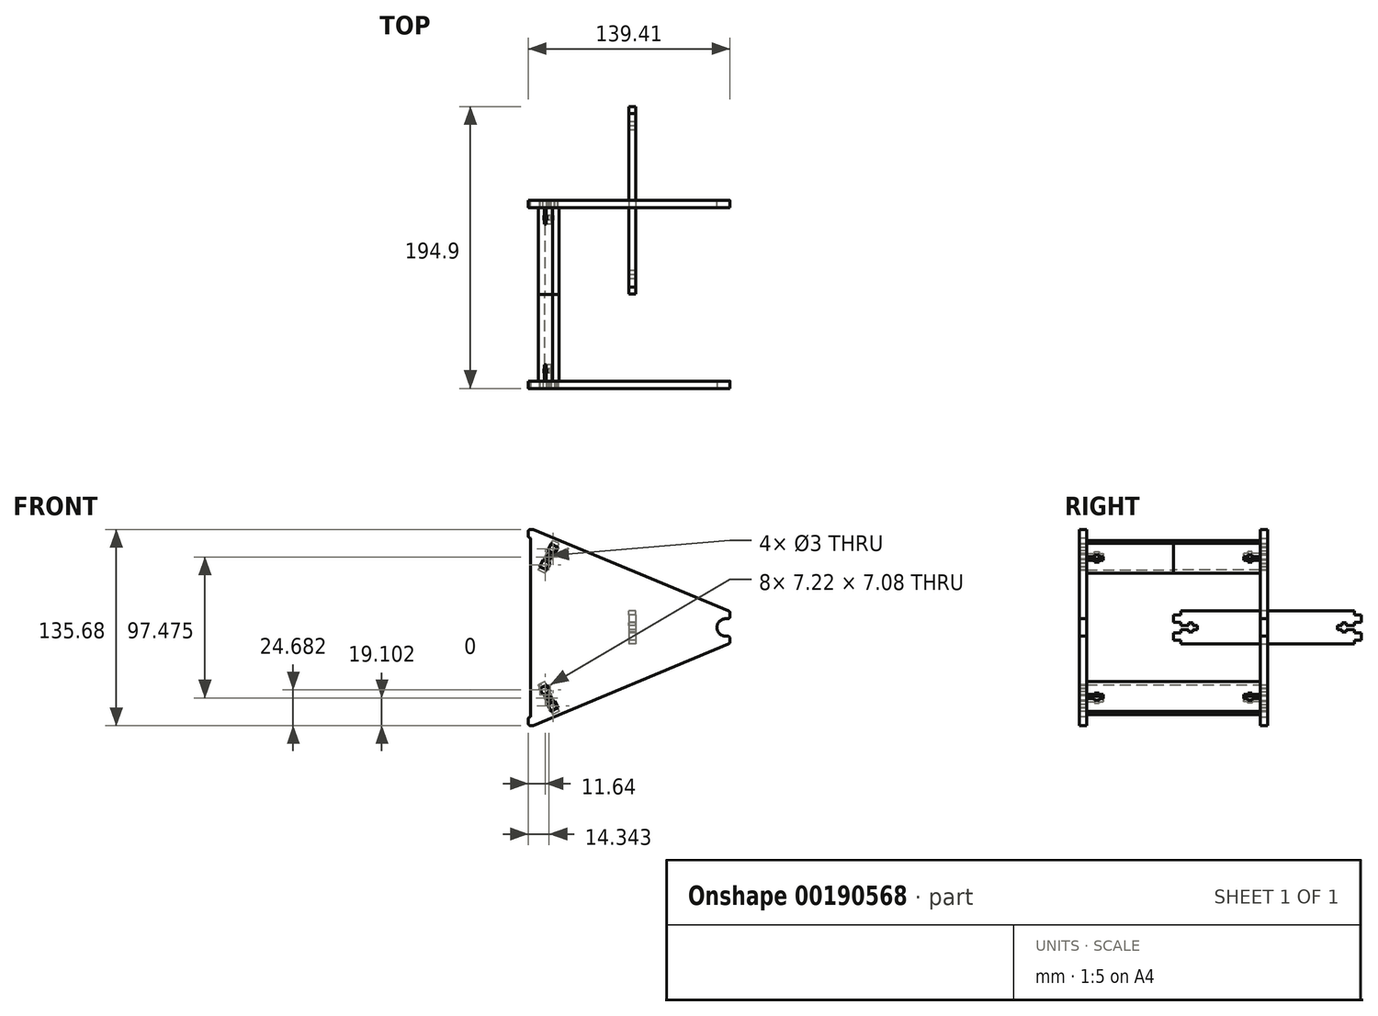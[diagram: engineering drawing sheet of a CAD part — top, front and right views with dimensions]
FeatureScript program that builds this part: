
annotation { "Feature Type Name" : "Feature", "Feature Type Description" : "" }
export const myFeature = defineFeature(function(context is Context, id is Id, definition is map)
    precondition{}
    {
        {
            var Q0;
            Q0=qCreatedBy(makeId("Front.planeOp"),FACE);
            var sketch = newSketch(context, id + "F0", { "sketchPlane" : qUnion([Q0])});
            skLineSegment(sketch, "E0.bottom", {"start": v(70, 69) * mm, "end": v(-70, 69) * mm, "construction": true});
            skLineSegment(sketch, "E0.top", {"start": v(70, -69) * mm, "end": v(-70, -69) * mm, "construction": true});
            skLineSegment(sketch, "E0.left", {"start": v(70, 69) * mm, "end": v(70, -69) * mm, "construction": true});
            skLineSegment(sketch, "E0.right", {"start": v(-70, 69) * mm, "end": v(-70, -69) * mm, "construction": true});
            skPoint(sketch, "E0.middle", {"position": v(0, 0) * mm});
            skLineSegment(sketch, "E1", {"start": v(-67.9, 67.84) * mm, "end": v(-66.66, 67.84) * mm});
            skLineSegment(sketch, "E2", {"start": v(-66.08, 67.72) * mm, "end": v(69.08, 11.47) * mm});
            skArc(sketch, "E3", {"start": v(67, 6) * mm, "mid": v(62.76, 4.24) * mm, "end": v(61, 0) * mm});
            skLineSegment(sketch, "E4", {"start": v(67, 6) * mm, "end": v(68.5, 6) * mm});
            skLineSegment(sketch, "E5", {"start": v(70, 7.5) * mm, "end": v(70, 10.09) * mm});
            skLineSegment(sketch, "E6", {"start": v(73.6, 0) * mm, "end": v(46.28, 0) * mm, "construction": true});
            skPoint(sketch, "E6.startSnap0", {"position": v(70, 0) * mm});
            skCircle(sketch, "E7", {"center": v(67, 0) * mm, "radius": 6 * mm, "construction": true});
            skCircle(sketch, "E8", {"center": v(45.57, 0) * mm, "radius": 27.5 * mm, "construction": true});
            skCircle(sketch, "E9", {"center": v(45.57, 0) * mm, "radius": 100 * mm, "construction": true});
            skLineSegment(sketch, "E10", {"start": v(-69.4, 66.34) * mm, "end": v(-69.4, 63.34) * mm});
            skLineSegment(sketch, "E11", {"start": v(-67.9, 61.84) * mm, "end": v(-67.9, 61.84) * mm});
            skLineSegment(sketch, "E12", {"start": v(-67.9, 61.84) * mm, "end": v(-67.9, 0) * mm});
            skPoint(sketch, "E13.visualSharp", {"position": v(70, 11.09) * mm});
            skArc(sketch, "E13.filletArc", {"start": v(70, 10.09) * mm, "mid": v(69.75, 10.92) * mm, "end": v(69.08, 11.47) * mm});
            skPoint(sketch, "E14.visualSharp", {"position": v(70, 6) * mm});
            skArc(sketch, "E14.filletArc", {"start": v(68.5, 6) * mm, "mid": v(69.56, 6.44) * mm, "end": v(70, 7.5) * mm});
            skPoint(sketch, "E15.visualSharp", {"position": v(-69.4, 67.84) * mm});
            skArc(sketch, "E15.filletArc", {"start": v(-67.9, 67.84) * mm, "mid": v(-68.97, 67.4) * mm, "end": v(-69.4, 66.34) * mm});
            skPoint(sketch, "E16.visualSharp", {"position": v(-69.4, 61.84) * mm});
            skArc(sketch, "E16.filletArc", {"start": v(-69.4, 63.34) * mm, "mid": v(-68.97, 62.27) * mm, "end": v(-67.9, 61.84) * mm});
            skPoint(sketch, "E17.visualSharp", {"position": v(-66.36, 67.84) * mm});
            skArc(sketch, "E17.filletArc", {"start": v(-66.08, 67.72) * mm, "mid": v(-66.37, 67.8) * mm, "end": v(-66.66, 67.84) * mm});
            skLineSegment(sketch, "E18", {"start": v(-48.76, 55.46) * mm, "end": v(-51.02, 50.78) * mm});
            skLineSegment(sketch, "E19", {"start": v(-37.94, 57) * mm, "end": v(-56.8, 18.07) * mm, "construction": true});
            skLineSegment(sketch, "E20", {"start": v(-48.76, 55.46) * mm, "end": v(-53.7, 57.86) * mm});
            skLineSegment(sketch, "E21", {"start": v(-56.43, 39.62) * mm, "end": v(-61.38, 42.02) * mm});
            skLineSegment(sketch, "E22", {"start": v(-53.7, 57.86) * mm, "end": v(-55.97, 53.18) * mm});
            skLineSegment(sketch, "E23", {"start": v(-57.54, 49.94) * mm, "end": v(-52.6, 47.54) * mm, "construction": true});
            skCircle(sketch, "E24", {"center": v(-55.07, 48.74) * mm, "radius": 1.5 * mm});
            skLineSegment(sketch, "E25", {"start": v(-55.97, 53.18) * mm, "end": v(-51.02, 50.78) * mm});
            skLineSegment(sketch, "E26.MirrorCS", {"start": v(-59.11, 46.7) * mm, "end": v(-54.16, 44.3) * mm});
            skLineSegment(sketch, "E27.trimOffspring", {"start": v(-54.16, 44.3) * mm, "end": v(-56.43, 39.62) * mm});
            skLineSegment(sketch, "E28.trimOffspring", {"start": v(-59.11, 46.7) * mm, "end": v(-61.38, 42.02) * mm});
            skLineSegment(sketch, "E29.MirrorCS", {"start": v(-66.08, -67.72) * mm, "end": v(69.08, -11.47) * mm});
            skArc(sketch, "E30.MirrorCS", {"start": v(-66.08, -67.72) * mm, "mid": v(-66.37, -67.8) * mm, "end": v(-66.66, -67.84) * mm});
            skLineSegment(sketch, "E31.MirrorCS", {"start": v(-67.9, -67.84) * mm, "end": v(-66.66, -67.84) * mm});
            skArc(sketch, "E32.MirrorCS", {"start": v(-67.9, -67.84) * mm, "mid": v(-68.97, -67.4) * mm, "end": v(-69.4, -66.34) * mm});
            skLineSegment(sketch, "E33.MirrorCS", {"start": v(-69.4, -66.34) * mm, "end": v(-69.4, -63.34) * mm});
            skArc(sketch, "E34.MirrorCS", {"start": v(-69.4, -63.34) * mm, "mid": v(-68.97, -62.27) * mm, "end": v(-67.9, -61.84) * mm});
            skLineSegment(sketch, "E35.MirrorCS", {"start": v(-67.9, -61.84) * mm, "end": v(-67.9, 0) * mm});
            skLineSegment(sketch, "E36.MirrorCS", {"start": v(70, -7.5) * mm, "end": v(70, -10.09) * mm});
            skArc(sketch, "E37.MirrorCS", {"start": v(70, -10.09) * mm, "mid": v(69.75, -10.92) * mm, "end": v(69.08, -11.47) * mm});
            skArc(sketch, "E38.MirrorCS", {"start": v(68.5, -6) * mm, "mid": v(69.56, -6.44) * mm, "end": v(70, -7.5) * mm});
            skLineSegment(sketch, "E39.MirrorCS", {"start": v(67, -6) * mm, "end": v(68.5, -6) * mm});
            skArc(sketch, "E40.MirrorCS", {"start": v(67, -6) * mm, "mid": v(62.76, -4.24) * mm, "end": v(61, 0) * mm});
            skLineSegment(sketch, "E41.MirrorCS", {"start": v(-57.54, -49.94) * mm, "end": v(-52.6, -47.54) * mm, "construction": true});
            skLineSegment(sketch, "E42.MirrorCS", {"start": v(-59.11, -46.7) * mm, "end": v(-61.38, -42.02) * mm});
            skLineSegment(sketch, "E43.MirrorCS", {"start": v(-53.7, -57.86) * mm, "end": v(-55.97, -53.18) * mm});
            skLineSegment(sketch, "E44.MirrorCS", {"start": v(-59.11, -46.7) * mm, "end": v(-54.16, -44.3) * mm});
            skLineSegment(sketch, "E45.MirrorCS", {"start": v(-55.97, -53.18) * mm, "end": v(-51.02, -50.78) * mm});
            skLineSegment(sketch, "E46.MirrorCS", {"start": v(-56.43, -39.62) * mm, "end": v(-61.38, -42.02) * mm});
            skCircle(sketch, "E47.MirrorC", {"center": v(-55.07, -48.74) * mm, "radius": 1.5 * mm});
            skLineSegment(sketch, "E48.MirrorCS", {"start": v(-48.76, -55.46) * mm, "end": v(-51.02, -50.78) * mm});
            skLineSegment(sketch, "E49.MirrorCS", {"start": v(-54.16, -44.3) * mm, "end": v(-56.43, -39.62) * mm});
            skLineSegment(sketch, "E50.MirrorCS", {"start": v(-48.76, -55.46) * mm, "end": v(-53.7, -57.86) * mm});
            skLineSegment(sketch, "E51", {"start": v(-48.76, 55.46) * mm, "end": v(-56.43, 39.62) * mm, "construction": true});
            skLineSegment(sketch, "E52", {"start": v(-52.6, 47.54) * mm, "end": v(45.57, 0) * mm, "construction": true});
            skSolve(sketch);
        }
        {
            var Q0;
            Q0 = qSketchRegion(id + "F0", true);
            extrude(context, id + "F1", {"entities" : qUnion([Q0]), "depth" : 5 * mm});
        }
        {
            var Q0;
            Q0=makeQuery(id+"F1.opExtrude","SWEPT_FACE",FACE,{"disambiguationData":[OSD([sQuery(id+"F0.wireOp",EDGE,"E43.MirrorCS")])]});
            var sketch = newSketch(context, id + "F2", { "sketchPlane" : qUnion([Q0])});
            skLineSegment(sketch, "E53", {"start": v(0, 0) * mm, "end": v(6.16, 29.6) * mm, "construction": true});
            skPoint(sketch, "E53.endSnap0", {"position": v(0, 29.6) * mm});
            skLineSegment(sketch, "E54.0", {"start": v(0, -18.36) * mm, "end": v(0, -21.36) * mm, "construction": true});
            skLineSegment(sketch, "E55", {"start": v(0, -19.86) * mm, "end": v(-5.02, -19.86) * mm, "construction": true});
            skLineSegment(sketch, "E56.1", {"start": v(-0.1, -16.16) * mm, "end": v(-0.1, -11.16) * mm});
            skLineSegment(sketch, "E56.2", {"start": v(-5, -16.16) * mm, "end": v(-0.1, -16.16) * mm});
            skLineSegment(sketch, "E57", {"start": v(-5, -16.16) * mm, "end": v(-5, -18.36) * mm});
            skLineSegment(sketch, "E58", {"start": v(-5, -18.36) * mm, "end": v(-10.6, -18.36) * mm});
            skLineSegment(sketch, "E59", {"start": v(-10.6, -18.36) * mm, "end": v(-10.6, -17.09) * mm});
            skLineSegment(sketch, "E60", {"start": v(-10.6, -17.09) * mm, "end": v(-13.5, -17.09) * mm});
            skLineSegment(sketch, "E61", {"start": v(-13.5, -17.09) * mm, "end": v(-13.5, -18.36) * mm});
            skLineSegment(sketch, "E62", {"start": v(-13.5, -18.36) * mm, "end": v(-16.5, -18.36) * mm});
            skLineSegment(sketch, "E63", {"start": v(-16.5, -18.36) * mm, "end": v(-16.5, -19.86) * mm});
            skLineSegment(sketch, "E64", {"start": v(-0.1, -11.16) * mm, "end": v(-5, -11.16) * mm});
            skLineSegment(sketch, "E65", {"start": v(-5, -11.16) * mm, "end": v(-5, -8.44) * mm});
            skLineSegment(sketch, "E66", {"start": v(-5, -8.44) * mm, "end": v(-65, -8.44) * mm});
            skLineSegment(sketch, "E67.MirrorCS", {"start": v(-13.5, -21.36) * mm, "end": v(-16.5, -21.36) * mm});
            skLineSegment(sketch, "E68.MirrorCS", {"start": v(-10.6, -21.36) * mm, "end": v(-10.6, -22.64) * mm});
            skLineSegment(sketch, "E69.MirrorCS", {"start": v(-5, -28.56) * mm, "end": v(-5, -31.28) * mm});
            skLineSegment(sketch, "E70.MirrorCS", {"start": v(-16.5, -21.36) * mm, "end": v(-16.5, -19.86) * mm});
            skLineSegment(sketch, "E71.MirrorCS", {"start": v(-5, -23.56) * mm, "end": v(-5, -21.36) * mm});
            skLineSegment(sketch, "E72.MirrorCS", {"start": v(-13.5, -22.64) * mm, "end": v(-13.5, -21.36) * mm});
            skLineSegment(sketch, "E73.MirrorCS", {"start": v(-10.6, -22.64) * mm, "end": v(-13.5, -22.64) * mm});
            skLineSegment(sketch, "E74.MirrorCS", {"start": v(0, -21.36) * mm, "end": v(0, -18.36) * mm, "construction": true});
            skLineSegment(sketch, "E75.MirrorCS", {"start": v(-5, -31.28) * mm, "end": v(-65, -31.28) * mm});
            skLineSegment(sketch, "E76.MirrorCS", {"start": v(-0.1, -23.56) * mm, "end": v(-0.1, -28.56) * mm});
            skLineSegment(sketch, "E77.MirrorCS", {"start": v(-5, -21.36) * mm, "end": v(-10.6, -21.36) * mm});
            skLineSegment(sketch, "E78.MirrorCS", {"start": v(-0.1, -28.56) * mm, "end": v(-5, -28.56) * mm});
            skLineSegment(sketch, "E79.MirrorCS", {"start": v(-5, -23.56) * mm, "end": v(-0.1, -23.56) * mm});
            skLineSegment(sketch, "E80", {"start": v(-65, -8.44) * mm, "end": v(-65, -31.28) * mm});
            skSolve(sketch);
        }
        {
            var Q0;
            Q0 = qSketchRegion(id + "F2", true);
            extrude(context, id + "F3", {"entities" : qUnion([Q0]), "depth" : 5 * mm});
        }
        {
            var Q0;
            Q0=makeQuery(id+"F3.opExtrude","SWEPT_BODY",BODY,{"disambiguationData":[OSD([sQuery(id+"F2.wireOp",EDGE,"E56.1"),sQuery(id+"F2.wireOp",EDGE,"E56.2"),sQuery(id+"F2.wireOp",EDGE,"E57"),sQuery(id+"F2.wireOp",EDGE,"E58"),sQuery(id+"F2.wireOp",EDGE,"E59"),sQuery(id+"F2.wireOp",EDGE,"E60"),sQuery(id+"F2.wireOp",EDGE,"E61"),sQuery(id+"F2.wireOp",EDGE,"E62"),sQuery(id+"F2.wireOp",EDGE,"E63"),sQuery(id+"F2.wireOp",EDGE,"E64"),sQuery(id+"F2.wireOp",EDGE,"E65"),sQuery(id+"F2.wireOp",EDGE,"E66"),sQuery(id+"F2.wireOp",EDGE,"E67.MirrorCS"),sQuery(id+"F2.wireOp",EDGE,"E68.MirrorCS"),sQuery(id+"F2.wireOp",EDGE,"E69.MirrorCS"),sQuery(id+"F2.wireOp",EDGE,"E70.MirrorCS"),sQuery(id+"F2.wireOp",EDGE,"E71.MirrorCS"),sQuery(id+"F2.wireOp",EDGE,"E72.MirrorCS"),sQuery(id+"F2.wireOp",EDGE,"E73.MirrorCS"),sQuery(id+"F2.wireOp",EDGE,"E75.MirrorCS"),sQuery(id+"F2.wireOp",EDGE,"E76.MirrorCS"),sQuery(id+"F2.wireOp",EDGE,"E77.MirrorCS"),sQuery(id+"F2.wireOp",EDGE,"E78.MirrorCS"),sQuery(id+"F2.wireOp",EDGE,"E79.MirrorCS"),sQuery(id+"F2.wireOp",EDGE,"E80")])]});
            var Q1;
            Q1=qCreatedBy(makeId("Top.planeOp"),FACE);
            mirror(context, id + "F4", {"entities" : qUnion([Q0]), "mirrorPlane" : qUnion([Q1])});
        }
        {
            var Q0;
            Q0=makeQuery(id+"F1.opExtrude","SWEPT_BODY",BODY,{"disambiguationData":[OSD([sQuery(id+"F0.wireOp",EDGE,"E1"),sQuery(id+"F0.wireOp",EDGE,"E2"),sQuery(id+"F0.wireOp",EDGE,"E3"),sQuery(id+"F0.wireOp",EDGE,"E4"),sQuery(id+"F0.wireOp",EDGE,"E5"),sQuery(id+"F0.wireOp",EDGE,"E10"),sQuery(id+"F0.wireOp",EDGE,"E12"),sQuery(id+"F0.wireOp",EDGE,"E13.filletArc"),sQuery(id+"F0.wireOp",EDGE,"E14.filletArc"),sQuery(id+"F0.wireOp",EDGE,"E15.filletArc"),sQuery(id+"F0.wireOp",EDGE,"E16.filletArc"),sQuery(id+"F0.wireOp",EDGE,"E17.filletArc"),sQuery(id+"F0.wireOp",EDGE,"E18"),sQuery(id+"F0.wireOp",EDGE,"E20"),sQuery(id+"F0.wireOp",EDGE,"E21"),sQuery(id+"F0.wireOp",EDGE,"E22"),sQuery(id+"F0.wireOp",EDGE,"E24"),sQuery(id+"F0.wireOp",EDGE,"E25"),sQuery(id+"F0.wireOp",EDGE,"E26.MirrorCS"),sQuery(id+"F0.wireOp",EDGE,"E27.trimOffspring"),sQuery(id+"F0.wireOp",EDGE,"E28.trimOffspring"),sQuery(id+"F0.wireOp",EDGE,"E29.MirrorCS"),sQuery(id+"F0.wireOp",EDGE,"E30.MirrorCS"),sQuery(id+"F0.wireOp",EDGE,"E31.MirrorCS"),sQuery(id+"F0.wireOp",EDGE,"E32.MirrorCS"),sQuery(id+"F0.wireOp",EDGE,"E33.MirrorCS"),sQuery(id+"F0.wireOp",EDGE,"E34.MirrorCS"),sQuery(id+"F0.wireOp",EDGE,"E35.MirrorCS"),sQuery(id+"F0.wireOp",EDGE,"E36.MirrorCS"),sQuery(id+"F0.wireOp",EDGE,"E37.MirrorCS"),sQuery(id+"F0.wireOp",EDGE,"E38.MirrorCS"),sQuery(id+"F0.wireOp",EDGE,"E39.MirrorCS"),sQuery(id+"F0.wireOp",EDGE,"E40.MirrorCS"),sQuery(id+"F0.wireOp",EDGE,"E42.MirrorCS"),sQuery(id+"F0.wireOp",EDGE,"E43.MirrorCS"),sQuery(id+"F0.wireOp",EDGE,"E44.MirrorCS"),sQuery(id+"F0.wireOp",EDGE,"E45.MirrorCS"),sQuery(id+"F0.wireOp",EDGE,"E46.MirrorCS"),sQuery(id+"F0.wireOp",EDGE,"E47.MirrorC"),sQuery(id+"F0.wireOp",EDGE,"E48.MirrorCS"),sQuery(id+"F0.wireOp",EDGE,"E49.MirrorCS"),sQuery(id+"F0.wireOp",EDGE,"E50.MirrorCS")])]});
            var Q1;
            Q1=makeQuery(id+"F3.opExtrude","SWEPT_BODY",BODY,{"disambiguationData":[OSD([sQuery(id+"F2.wireOp",EDGE,"E56.1"),sQuery(id+"F2.wireOp",EDGE,"E56.2"),sQuery(id+"F2.wireOp",EDGE,"E57"),sQuery(id+"F2.wireOp",EDGE,"E58"),sQuery(id+"F2.wireOp",EDGE,"E59"),sQuery(id+"F2.wireOp",EDGE,"E60"),sQuery(id+"F2.wireOp",EDGE,"E61"),sQuery(id+"F2.wireOp",EDGE,"E62"),sQuery(id+"F2.wireOp",EDGE,"E63"),sQuery(id+"F2.wireOp",EDGE,"E64"),sQuery(id+"F2.wireOp",EDGE,"E65"),sQuery(id+"F2.wireOp",EDGE,"E66"),sQuery(id+"F2.wireOp",EDGE,"E67.MirrorCS"),sQuery(id+"F2.wireOp",EDGE,"E68.MirrorCS"),sQuery(id+"F2.wireOp",EDGE,"E69.MirrorCS"),sQuery(id+"F2.wireOp",EDGE,"E70.MirrorCS"),sQuery(id+"F2.wireOp",EDGE,"E71.MirrorCS"),sQuery(id+"F2.wireOp",EDGE,"E72.MirrorCS"),sQuery(id+"F2.wireOp",EDGE,"E73.MirrorCS"),sQuery(id+"F2.wireOp",EDGE,"E75.MirrorCS"),sQuery(id+"F2.wireOp",EDGE,"E76.MirrorCS"),sQuery(id+"F2.wireOp",EDGE,"E77.MirrorCS"),sQuery(id+"F2.wireOp",EDGE,"E78.MirrorCS"),sQuery(id+"F2.wireOp",EDGE,"E79.MirrorCS"),sQuery(id+"F2.wireOp",EDGE,"E80")])]});
            var Q2;
            Q2=makeQuery(id+"F4.opPattern","COPY",BODY,{"derivedFrom":makeQuery(id+"F3.opExtrude","SWEPT_BODY",BODY,{"disambiguationData":[OSD([sQuery(id+"F2.wireOp",EDGE,"E56.1"),sQuery(id+"F2.wireOp",EDGE,"E56.2"),sQuery(id+"F2.wireOp",EDGE,"E57"),sQuery(id+"F2.wireOp",EDGE,"E58"),sQuery(id+"F2.wireOp",EDGE,"E59"),sQuery(id+"F2.wireOp",EDGE,"E60"),sQuery(id+"F2.wireOp",EDGE,"E61"),sQuery(id+"F2.wireOp",EDGE,"E62"),sQuery(id+"F2.wireOp",EDGE,"E63"),sQuery(id+"F2.wireOp",EDGE,"E64"),sQuery(id+"F2.wireOp",EDGE,"E65"),sQuery(id+"F2.wireOp",EDGE,"E66"),sQuery(id+"F2.wireOp",EDGE,"E67.MirrorCS"),sQuery(id+"F2.wireOp",EDGE,"E68.MirrorCS"),sQuery(id+"F2.wireOp",EDGE,"E69.MirrorCS"),sQuery(id+"F2.wireOp",EDGE,"E70.MirrorCS"),sQuery(id+"F2.wireOp",EDGE,"E71.MirrorCS"),sQuery(id+"F2.wireOp",EDGE,"E72.MirrorCS"),sQuery(id+"F2.wireOp",EDGE,"E73.MirrorCS"),sQuery(id+"F2.wireOp",EDGE,"E75.MirrorCS"),sQuery(id+"F2.wireOp",EDGE,"E76.MirrorCS"),sQuery(id+"F2.wireOp",EDGE,"E77.MirrorCS"),sQuery(id+"F2.wireOp",EDGE,"E78.MirrorCS"),sQuery(id+"F2.wireOp",EDGE,"E79.MirrorCS"),sQuery(id+"F2.wireOp",EDGE,"E80")])]}),"instanceName":"1"});
            var Q3;
            Q3=makeQuery(id+"F4.opPattern","COPY",FACE,{"derivedFrom":makeQuery(id+"F3.opExtrude","SWEPT_FACE",FACE,{"disambiguationData":[OSD([sQuery(id+"F2.wireOp",EDGE,"E80")])]}),"instanceName":"1"});
            mirror(context, id + "F5", {"entities" : qUnion([Q0, Q1, Q2]), "mirrorPlane" : qUnion([Q3])});
        }
        {
            var Q0;
            Q0=makeQuery(id+"F5.opPattern","COPY",BODY,{"derivedFrom":makeQuery(id+"F3.opExtrude","SWEPT_BODY",BODY,{"disambiguationData":[OSD([sQuery(id+"F2.wireOp",EDGE,"E56.1"),sQuery(id+"F2.wireOp",EDGE,"E56.2"),sQuery(id+"F2.wireOp",EDGE,"E57"),sQuery(id+"F2.wireOp",EDGE,"E58"),sQuery(id+"F2.wireOp",EDGE,"E59"),sQuery(id+"F2.wireOp",EDGE,"E60"),sQuery(id+"F2.wireOp",EDGE,"E61"),sQuery(id+"F2.wireOp",EDGE,"E62"),sQuery(id+"F2.wireOp",EDGE,"E63"),sQuery(id+"F2.wireOp",EDGE,"E64"),sQuery(id+"F2.wireOp",EDGE,"E65"),sQuery(id+"F2.wireOp",EDGE,"E66"),sQuery(id+"F2.wireOp",EDGE,"E67.MirrorCS"),sQuery(id+"F2.wireOp",EDGE,"E68.MirrorCS"),sQuery(id+"F2.wireOp",EDGE,"E69.MirrorCS"),sQuery(id+"F2.wireOp",EDGE,"E70.MirrorCS"),sQuery(id+"F2.wireOp",EDGE,"E71.MirrorCS"),sQuery(id+"F2.wireOp",EDGE,"E72.MirrorCS"),sQuery(id+"F2.wireOp",EDGE,"E73.MirrorCS"),sQuery(id+"F2.wireOp",EDGE,"E75.MirrorCS"),sQuery(id+"F2.wireOp",EDGE,"E76.MirrorCS"),sQuery(id+"F2.wireOp",EDGE,"E77.MirrorCS"),sQuery(id+"F2.wireOp",EDGE,"E78.MirrorCS"),sQuery(id+"F2.wireOp",EDGE,"E79.MirrorCS"),sQuery(id+"F2.wireOp",EDGE,"E80")])]}),"instanceName":"1"});
            var Q1;
            Q1=makeQuery(id+"F3.opExtrude","SWEPT_BODY",BODY,{"disambiguationData":[OSD([sQuery(id+"F2.wireOp",EDGE,"E56.1"),sQuery(id+"F2.wireOp",EDGE,"E56.2"),sQuery(id+"F2.wireOp",EDGE,"E57"),sQuery(id+"F2.wireOp",EDGE,"E58"),sQuery(id+"F2.wireOp",EDGE,"E59"),sQuery(id+"F2.wireOp",EDGE,"E60"),sQuery(id+"F2.wireOp",EDGE,"E61"),sQuery(id+"F2.wireOp",EDGE,"E62"),sQuery(id+"F2.wireOp",EDGE,"E63"),sQuery(id+"F2.wireOp",EDGE,"E64"),sQuery(id+"F2.wireOp",EDGE,"E65"),sQuery(id+"F2.wireOp",EDGE,"E66"),sQuery(id+"F2.wireOp",EDGE,"E67.MirrorCS"),sQuery(id+"F2.wireOp",EDGE,"E68.MirrorCS"),sQuery(id+"F2.wireOp",EDGE,"E69.MirrorCS"),sQuery(id+"F2.wireOp",EDGE,"E70.MirrorCS"),sQuery(id+"F2.wireOp",EDGE,"E71.MirrorCS"),sQuery(id+"F2.wireOp",EDGE,"E72.MirrorCS"),sQuery(id+"F2.wireOp",EDGE,"E73.MirrorCS"),sQuery(id+"F2.wireOp",EDGE,"E75.MirrorCS"),sQuery(id+"F2.wireOp",EDGE,"E76.MirrorCS"),sQuery(id+"F2.wireOp",EDGE,"E77.MirrorCS"),sQuery(id+"F2.wireOp",EDGE,"E78.MirrorCS"),sQuery(id+"F2.wireOp",EDGE,"E79.MirrorCS"),sQuery(id+"F2.wireOp",EDGE,"E80")])]});
            booleanBodies(context, id + "F6", {"operationType" : BooleanOperationType.UNION, "tools" : qUnion([Q0, Q1])});
        }
        {
            var Q0;
            Q0=qCreatedBy(makeId("Right.planeOp"),FACE);
            var sketch = newSketch(context, id + "F7", { "sketchPlane" : qUnion([Q0])});
            skLineSegment(sketch, "E81.0.0", {"start": v(-64.9, 3.7) * mm, "end": v(-60, 3.7) * mm});
            skLineSegment(sketch, "E81.0.1", {"start": v(-60, 3.7) * mm, "end": v(-60, 1.5) * mm});
            skLineSegment(sketch, "E81.0.2", {"start": v(-60, 1.5) * mm, "end": v(-54.4, 1.5) * mm});
            skLineSegment(sketch, "E81.0.3", {"start": v(-54.4, 1.5) * mm, "end": v(-54.4, 3.18) * mm});
            skLineSegment(sketch, "E81.0.4", {"start": v(-54.4, 3.18) * mm, "end": v(-51.5, 3.18) * mm});
            skLineSegment(sketch, "E81.0.5", {"start": v(-51.5, 3.18) * mm, "end": v(-51.5, 1.5) * mm});
            skLineSegment(sketch, "E81.0.6", {"start": v(-51.5, 1.5) * mm, "end": v(-48.5, 1.5) * mm});
            skLineSegment(sketch, "E81.0.7", {"start": v(-48.5, 1.5) * mm, "end": v(-48.5, -1.5) * mm});
            skLineSegment(sketch, "E81.0.8", {"start": v(-48.5, -1.5) * mm, "end": v(-51.5, -1.5) * mm});
            skLineSegment(sketch, "E81.0.9", {"start": v(-51.5, -1.5) * mm, "end": v(-51.5, -3.18) * mm});
            skLineSegment(sketch, "E81.0.10", {"start": v(-51.5, -3.18) * mm, "end": v(-54.4, -3.18) * mm});
            skLineSegment(sketch, "E81.0.11", {"start": v(-54.4, -3.18) * mm, "end": v(-54.4, -1.5) * mm});
            skLineSegment(sketch, "E81.0.12", {"start": v(-54.4, -1.5) * mm, "end": v(-60, -1.5) * mm});
            skLineSegment(sketch, "E81.0.13", {"start": v(-60, -1.5) * mm, "end": v(-60, -3.7) * mm});
            skLineSegment(sketch, "E81.0.14", {"start": v(-60, -3.7) * mm, "end": v(-64.9, -3.7) * mm});
            skLineSegment(sketch, "E81.0.15", {"start": v(-64.9, -3.7) * mm, "end": v(-64.9, -8.7) * mm});
            skLineSegment(sketch, "E81.0.16", {"start": v(-64.9, -8.7) * mm, "end": v(-60, -8.7) * mm});
            skLineSegment(sketch, "E81.0.17", {"start": v(-60, -8.7) * mm, "end": v(-60, -11.42) * mm});
            skLineSegment(sketch, "E81.0.18", {"start": v(-60, -11.42) * mm, "end": v(60, -11.42) * mm});
            skLineSegment(sketch, "E81.0.19", {"start": v(60, -11.42) * mm, "end": v(60, -8.7) * mm});
            skLineSegment(sketch, "E81.0.20", {"start": v(60, -8.7) * mm, "end": v(64.9, -8.7) * mm});
            skLineSegment(sketch, "E81.0.21", {"start": v(64.9, -8.7) * mm, "end": v(64.9, -3.7) * mm});
            skLineSegment(sketch, "E81.0.22", {"start": v(64.9, -3.7) * mm, "end": v(60, -3.7) * mm});
            skLineSegment(sketch, "E81.0.23", {"start": v(60, -3.7) * mm, "end": v(60, -1.5) * mm});
            skLineSegment(sketch, "E81.0.24", {"start": v(60, -1.5) * mm, "end": v(54.4, -1.5) * mm});
            skLineSegment(sketch, "E81.0.25", {"start": v(54.4, -1.5) * mm, "end": v(54.4, -3.18) * mm});
            skLineSegment(sketch, "E81.0.26", {"start": v(54.4, -3.18) * mm, "end": v(51.5, -3.18) * mm});
            skLineSegment(sketch, "E81.0.27", {"start": v(51.5, -3.18) * mm, "end": v(51.5, -1.5) * mm});
            skLineSegment(sketch, "E81.0.28", {"start": v(51.5, -1.5) * mm, "end": v(48.5, -1.5) * mm});
            skLineSegment(sketch, "E81.0.29", {"start": v(48.5, -1.5) * mm, "end": v(48.5, 1.5) * mm});
            skLineSegment(sketch, "E81.0.30", {"start": v(48.5, 1.5) * mm, "end": v(51.5, 1.5) * mm});
            skLineSegment(sketch, "E81.0.31", {"start": v(51.5, 1.5) * mm, "end": v(51.5, 3.18) * mm});
            skLineSegment(sketch, "E81.0.32", {"start": v(51.5, 3.18) * mm, "end": v(54.4, 3.18) * mm});
            skLineSegment(sketch, "E81.0.33", {"start": v(54.4, 3.18) * mm, "end": v(54.4, 1.5) * mm});
            skLineSegment(sketch, "E81.0.34", {"start": v(54.4, 1.5) * mm, "end": v(60, 1.5) * mm});
            skLineSegment(sketch, "E81.0.35", {"start": v(60, 1.5) * mm, "end": v(60, 3.7) * mm});
            skLineSegment(sketch, "E81.0.36", {"start": v(60, 3.7) * mm, "end": v(64.9, 3.7) * mm});
            skLineSegment(sketch, "E81.0.37", {"start": v(64.9, 3.7) * mm, "end": v(64.9, 8.7) * mm});
            skLineSegment(sketch, "E81.0.38", {"start": v(64.9, 8.7) * mm, "end": v(60, 8.7) * mm});
            skLineSegment(sketch, "E81.0.39", {"start": v(60, 8.7) * mm, "end": v(60, 11.42) * mm});
            skLineSegment(sketch, "E81.0.40", {"start": v(60, 11.42) * mm, "end": v(-60, 11.42) * mm});
            skLineSegment(sketch, "E81.0.41", {"start": v(-60, 11.42) * mm, "end": v(-60, 8.7) * mm});
            skLineSegment(sketch, "E81.0.42", {"start": v(-60, 8.7) * mm, "end": v(-64.9, 8.7) * mm});
            skLineSegment(sketch, "E81.0.43", {"start": v(-64.9, 8.7) * mm, "end": v(-64.9, 3.7) * mm});
            skSolve(sketch);
        }
        {
            var Q0;
            Q0=makeQuery(id+"F7.imprint","IMPRINT",FACE,{"disambiguationData":[TD([[makeQuery(id+"F7.imprint","IMPRINT",EDGE,{"derivedFrom":sQuery(id+"F7.wireOp",EDGE,"E81.0.0")}),1.0]])]});
            extrude(context, id + "F8", {"entities" : qUnion([Q0]), "depth" : 5 * mm});
        }
    });
